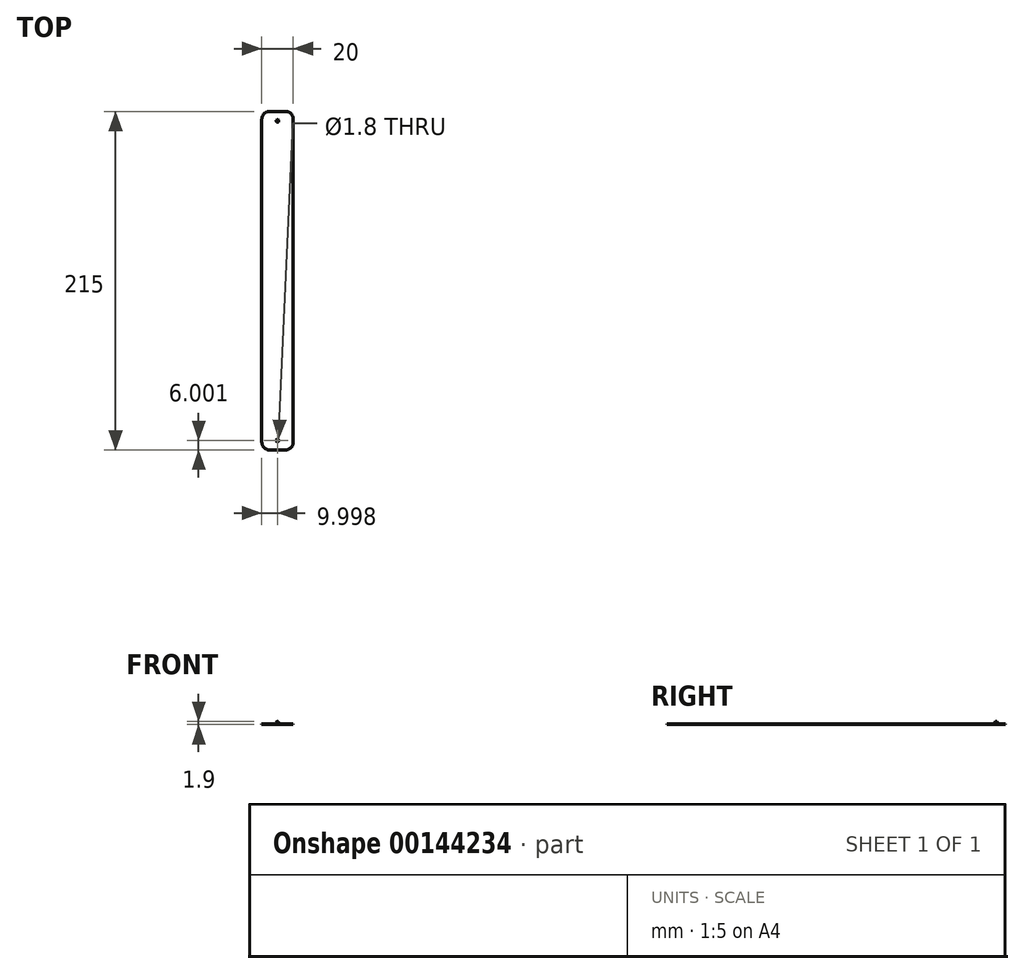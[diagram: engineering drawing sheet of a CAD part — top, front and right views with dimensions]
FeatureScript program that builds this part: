
annotation { "Feature Type Name" : "Feature", "Feature Type Description" : "" }
export const myFeature = defineFeature(function(context is Context, id is Id, definition is map)
    precondition{}
    {
        {
            var Q0;
            Q0=qCreatedBy(makeId("Top.planeOp"),FACE);
            var sketch = newSketch(context, id + "F0", { "sketchPlane" : qUnion([Q0])});
            skLineSegment(sketch, "E0.bottom", {"start": v(-16.54, 67.66) * mm, "end": v(-6.54, 67.66) * mm});
            skLineSegment(sketch, "E0.top", {"start": v(-16.54, -147.34) * mm, "end": v(-6.54, -147.34) * mm});
            skLineSegment(sketch, "E0.left", {"start": v(-21.54, 62.66) * mm, "end": v(-21.54, -142.34) * mm});
            skLineSegment(sketch, "E0.right", {"start": v(-1.54, 62.66) * mm, "end": v(-1.54, -142.34) * mm});
            skPoint(sketch, "E1.visualSharp", {"position": v(-21.54, -147.34) * mm});
            skArc(sketch, "E1.filletArc", {"start": v(-21.54, -142.34) * mm, "mid": v(-20.08, -145.87) * mm, "end": v(-16.54, -147.34) * mm});
            skPoint(sketch, "E2.visualSharp", {"position": v(-1.54, -147.34) * mm});
            skArc(sketch, "E2.filletArc", {"start": v(-6.54, -147.34) * mm, "mid": v(-3, -145.87) * mm, "end": v(-1.54, -142.34) * mm});
            skPoint(sketch, "E3.visualSharp", {"position": v(-1.54, 67.66) * mm});
            skArc(sketch, "E3.filletArc", {"start": v(-1.54, 62.66) * mm, "mid": v(-3, 66.2) * mm, "end": v(-6.54, 67.66) * mm});
            skPoint(sketch, "E4.visualSharp", {"position": v(-21.54, 67.66) * mm});
            skArc(sketch, "E4.filletArc", {"start": v(-16.54, 67.66) * mm, "mid": v(-20.08, 66.2) * mm, "end": v(-21.54, 62.66) * mm});
            skSolve(sketch);
        }
        {
            var Q0;
            Q0=qSketchRegion(id+"F0",true);
            extrude(context, id + "F1", {"entities" : qUnion([Q0]), "depth" : 0.4 * mm});
        }
        {
            var Q0;
            Q0=makeQuery(id+"F1.opExtrude","CAP_FACE",FACE,{"disambiguationData":[OSD([sQuery(id+"F0.wireOp",EDGE,"E0.bottom"),sQuery(id+"F0.wireOp",EDGE,"E0.top"),sQuery(id+"F0.wireOp",EDGE,"E0.left"),sQuery(id+"F0.wireOp",EDGE,"E0.right"),sQuery(id+"F0.wireOp",EDGE,"E1.filletArc"),sQuery(id+"F0.wireOp",EDGE,"E2.filletArc"),sQuery(id+"F0.wireOp",EDGE,"E3.filletArc"),sQuery(id+"F0.wireOp",EDGE,"E4.filletArc")])],"isStart":false});
            var sketch = newSketch(context, id + "F2", { "sketchPlane" : qUnion([Q0])});
            skCircle(sketch, "E5", {"center": v(-11.54, 61.66) * mm, "radius": 0.75 * mm});
            skPoint(sketch, "E5.centerSnap0", {"position": v(-11.54, 67.66) * mm});
            skPoint(sketch, "E6", {"position": v(-11.54, -141.34) * mm});
            skPoint(sketch, "E6.positionSnap0", {"position": v(-11.54, -147.34) * mm});
            skSolve(sketch);
        }
        {
            var Q0;
            Q0=qSketchRegion(id+"F2",true);
            extrude(context, id + "F3", {"entities" : qUnion([Q0]), "operationType" : NewBodyOperationType.ADD, "offsetDistance" : 25 * mm, "depth" : 1.5 * mm, "hasDraft" : true, "draftAngle" : 3 * degree});
        }
        {
            var Q0;
            Q0=makeQuery(id+"F3.opExtrude","CAP_FACE",FACE,{"disambiguationData":[OSD([sQuery(id+"F2.wireOp",EDGE,"E5")])],"isStart":false});
            chamfer(context, id + "F4", {"entities" : qUnion([Q0]), "width" : 0.4 * mm, "tangentPropagation" : true});
        }
        {
            var Q0;
            Q0=sQuery(id+"F2.wireOp",VERTEX,"E6");
            var Q1;
            Q1=makeQuery(id+"F1.opExtrude","SWEPT_BODY",BODY,{"disambiguationData":[OSD([sQuery(id+"F0.wireOp",EDGE,"E0.bottom"),sQuery(id+"F0.wireOp",EDGE,"E0.top"),sQuery(id+"F0.wireOp",EDGE,"E0.left"),sQuery(id+"F0.wireOp",EDGE,"E0.right"),sQuery(id+"F0.wireOp",EDGE,"E1.filletArc"),sQuery(id+"F0.wireOp",EDGE,"E2.filletArc"),sQuery(id+"F0.wireOp",EDGE,"E3.filletArc"),sQuery(id+"F0.wireOp",EDGE,"E4.filletArc")])]});
            hole(context, id + "F5", {"style" : HoleStyle.SIMPLE, "endStyle" : HoleEndStyle.THROUGH, "holeDiameter" : 1.8 * mm, "majorDiameter" : 5 * mm, "isTappedThrough" : true, "tappedDepth" : 12 * mm, "tapClearance" : 3, "locations" : qUnion([Q0]), "scope" : qUnion([Q1])});
        }
    });
